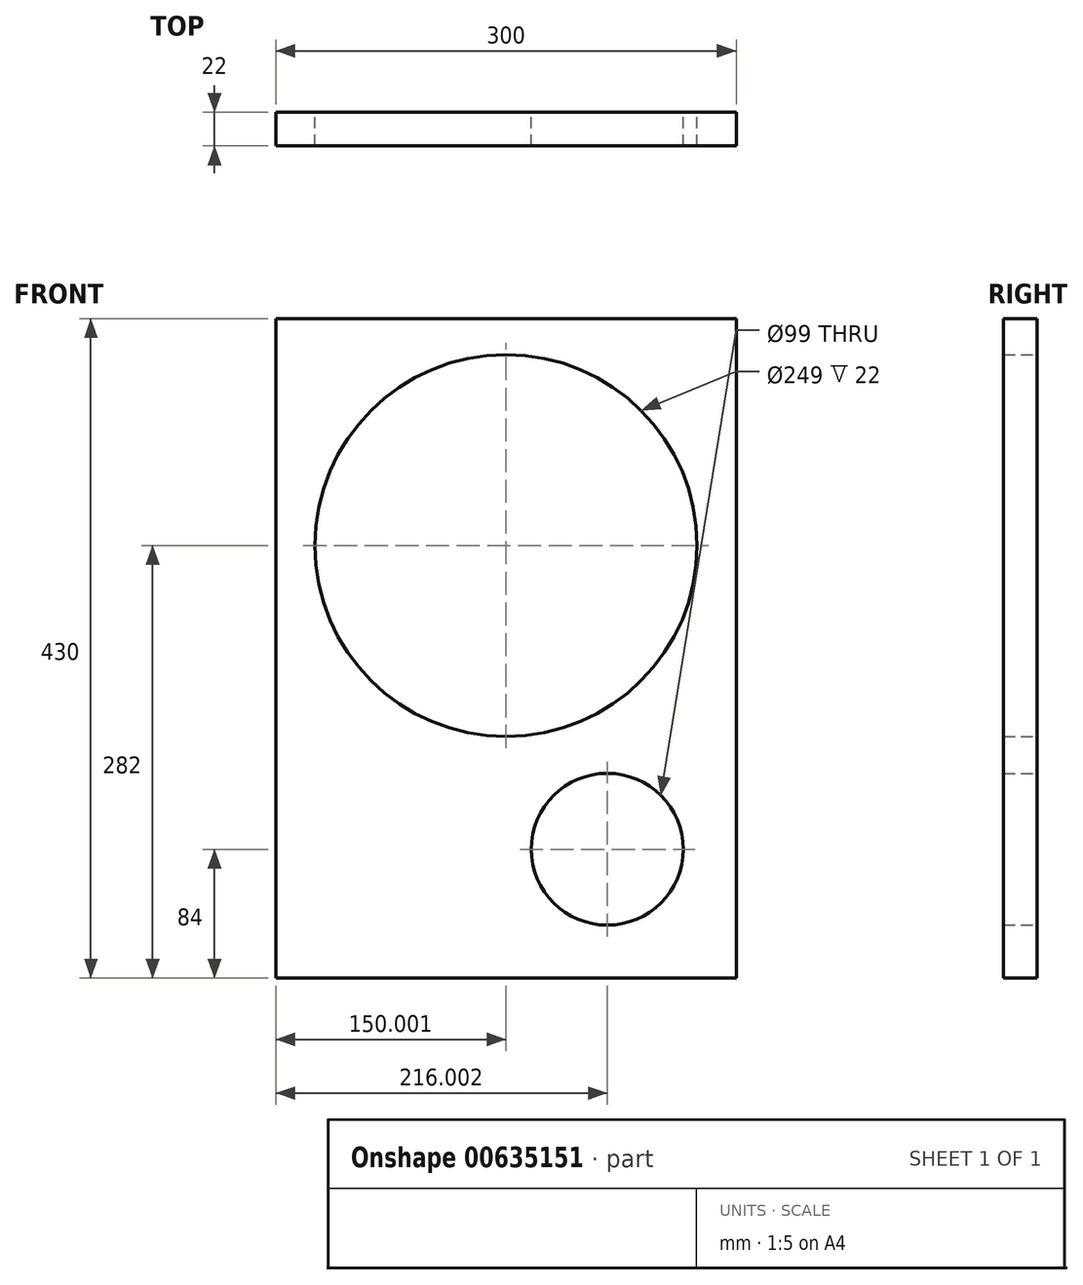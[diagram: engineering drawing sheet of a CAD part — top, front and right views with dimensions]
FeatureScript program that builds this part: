
annotation { "Feature Type Name" : "Feature", "Feature Type Description" : "" }
export const myFeature = defineFeature(function(context is Context, id is Id, definition is map)
    precondition{}
    {
        {
            var Q0;
            Q0=qCreatedBy(makeId("Front.planeOp"),FACE);
            var sketch = newSketch(context, id + "F0", { "sketchPlane" : qUnion([Q0])});
            skLineSegment(sketch, "E0.bottom", {"start": v(-115.8, 0) * mm, "end": v(184.2, 0) * mm});
            skLineSegment(sketch, "E0.top", {"start": v(-115.8, 430) * mm, "end": v(184.2, 430) * mm});
            skLineSegment(sketch, "E0.left", {"start": v(-115.8, 0) * mm, "end": v(-115.8, 430) * mm});
            skLineSegment(sketch, "E0.right", {"start": v(184.2, 0) * mm, "end": v(184.2, 430) * mm});
            skCircle(sketch, "E1", {"center": v(100.2, 84) * mm, "radius": 49.5 * mm});
            skCircle(sketch, "E2", {"center": v(34.2, 282) * mm, "radius": 124.5 * mm});
            skCircle(sketch, "E3", {"center": v(34.2, 282) * mm, "radius": 145 * mm, "construction": true});
            skCircle(sketch, "E4", {"center": v(100.2, 84) * mm, "radius": 59 * mm, "construction": true});
            skSolve(sketch);
        }
        {
            var Q0;
            Q0=makeQuery(id+"F0.imprint","IMPRINT",FACE,{"disambiguationData":[TD([[makeQuery(id+"F0.imprint","IMPRINT",EDGE,{"derivedFrom":sQuery(id+"F0.wireOp",EDGE,"E0.bottom")}),1.0]])]});
            extrude(context, id + "F1", {"entities" : qUnion([Q0]), "depth" : 22 * mm, "offsetDistance" : 25 * mm});
        }
    });
